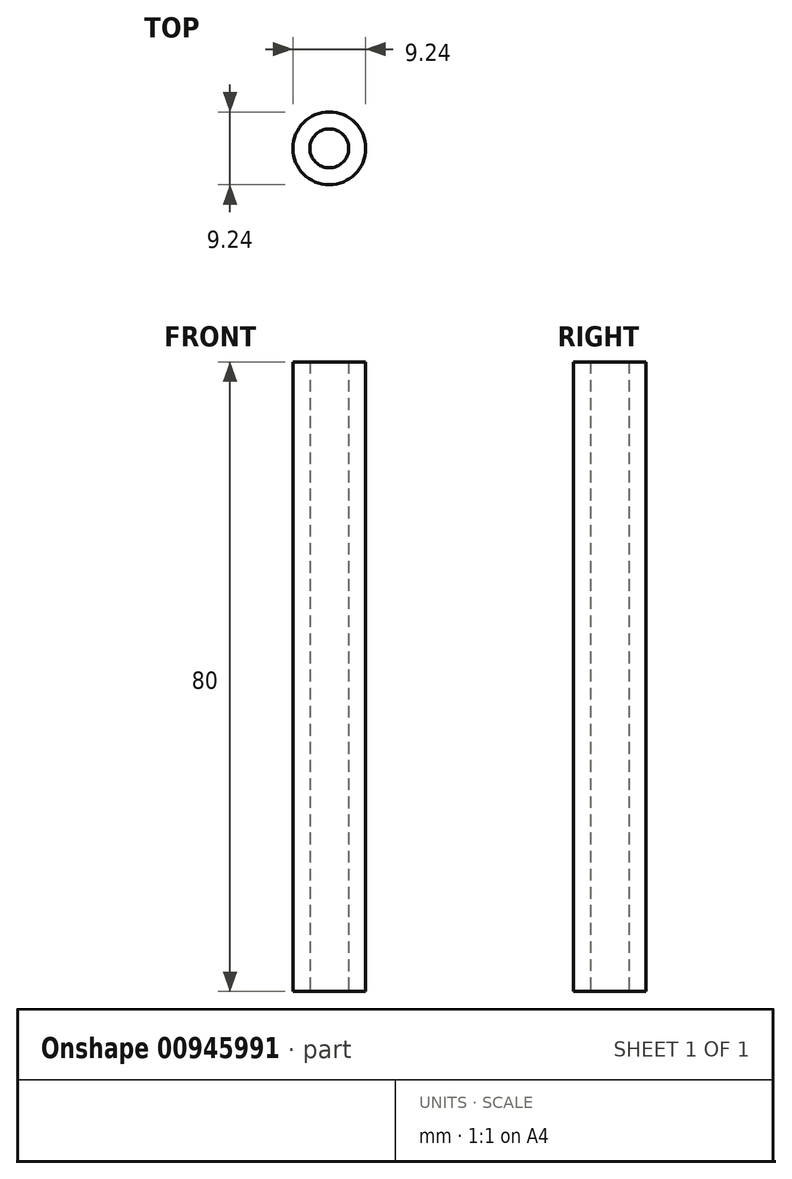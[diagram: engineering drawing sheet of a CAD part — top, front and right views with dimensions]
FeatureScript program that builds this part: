
annotation { "Feature Type Name" : "Feature", "Feature Type Description" : "" }
export const myFeature = defineFeature(function(context is Context, id is Id, definition is map)
    precondition{}
    {
        {
            var Q0;
            Q0=qCreatedBy(makeId("Top.planeOp"),FACE);
            var sketch = newSketch(context, id + "F0", { "sketchPlane" : qUnion([Q0])});
            skCircle(sketch, "E0", {"center": v(0, 0) * mm, "radius": 2.47 * mm});
            skSolve(sketch);
        }
        {
            var Q0;
            Q0=qCreatedBy(makeId("Top.planeOp"),FACE);
            var sketch = newSketch(context, id + "F1", { "sketchPlane" : qUnion([Q0])});
            skCircle(sketch, "E1", {"center": v(0, 0) * mm, "radius": 4.62 * mm});
            skSolve(sketch);
        }
        {
            var Q0;
            Q0=makeQuery(id+"F1.imprint","IMPRINT",FACE,{"disambiguationData":[TD([[makeQuery(id+"F1.imprint","IMPRINT",EDGE,{"derivedFrom":sQuery(id+"F1.wireOp",EDGE,"E1")}),1.0]])]});
            var Q1;
            Q1 = qSketchRegion(id + "F0", true);
            extrude(context, id + "F2", {"entities" : qUnion([Q0, Q1]), "depth" : 80 * mm, "offsetDistance" : 25 * mm});
        }
    });
